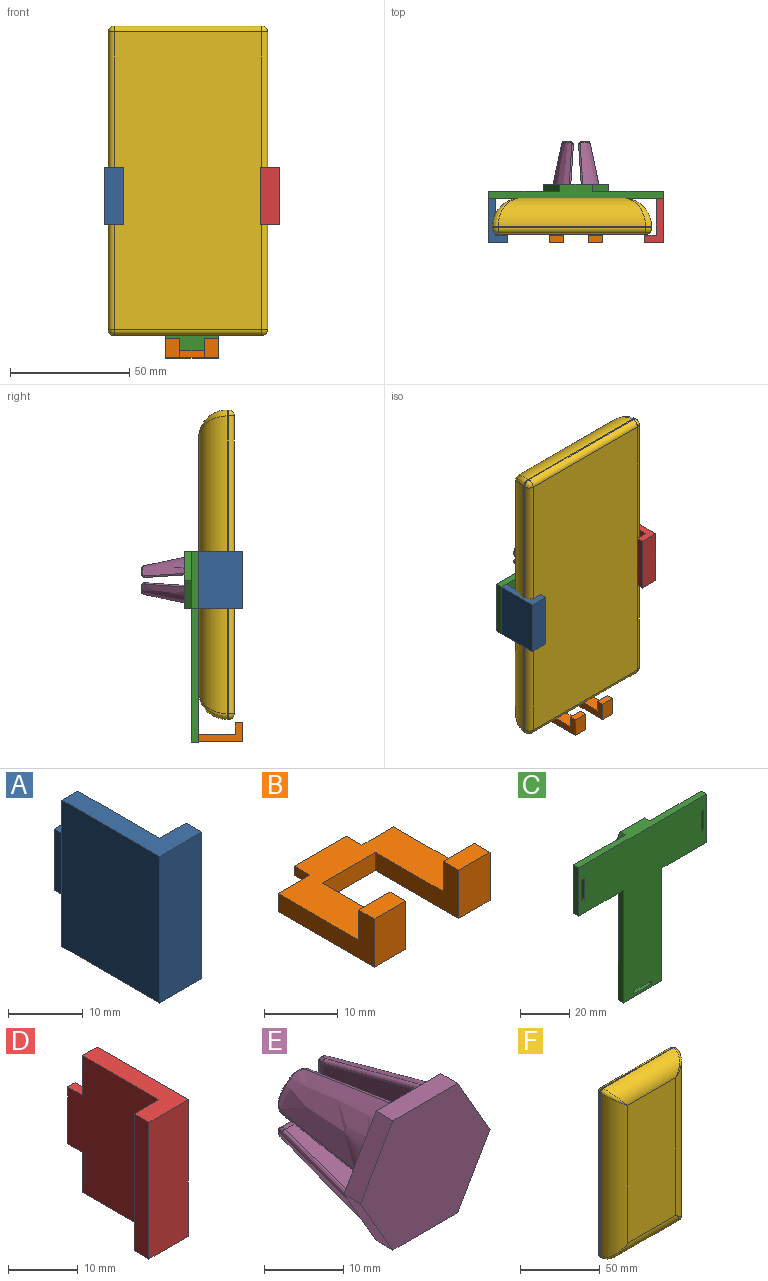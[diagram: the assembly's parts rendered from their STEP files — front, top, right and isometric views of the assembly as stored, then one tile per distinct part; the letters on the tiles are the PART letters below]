
ASSEMBLY  parts=6 mates=5
PART A: 12 faces, bbox 8x21.5x24 mm
  f0: plane 18.5x8mm, normal (0,0,-1), area 70.5mm2, adj f1,f4,f5,f6,f7,f11
  f1: plane 24x18.5mm, normal (1,0,0), area 402mm2, adj f0,f2,f3,f7,f8,f10,f11
  f2: plane 18.5x8mm, normal (0,0,1), area 70.5mm2, adj f1,f4,f5,f6,f7,f11
  f3: plane 10x1.5mm, normal (0,1,0), area 15mm2, adj f1,f8,f9,f10
  f4: plane 24x18.5mm, normal (-1,0,0), area 444mm2, adj f0,f2,f6,f11
  f5: plane 24x3mm, normal (1,0,0), area 72mm2, adj f0,f2,f6,f7
  f6: plane 24x8mm, normal (0,-1,0), area 192mm2, adj f0,f2,f4,f5
  f7: plane 24x5mm, normal (0,1,0), area 120mm2, adj f0,f1,f2,f5
  f8: plane 3x1.5mm, normal (0,0,1), area 4.5mm2, adj f1,f3,f9,f11
  f9: plane 10x3mm, normal (-1,0,0), area 30mm2, adj f3,f8,f10,f11
  f10: plane 3x1.5mm, normal (0,0,-1), area 4.5mm2, adj f1,f3,f9,f11
  f11: plane 24x3mm, normal (0,1,0), area 57mm2, adj f0,f1,f2,f4,f8,f9,f10
PART B: 18 faces, bbox 22.2x21.5x8 mm
  f0: plane 10x1.5mm, normal (0,1,0), area 15mm2, adj f1,f2,f3,f4
  f1: plane 22.2x18.5mm, normal (0,0,1), area 241.5mm2, adj f0,f3,f4,f5,f6,f7,f9,f12
  f2: plane 10x3mm, normal (0,0,-1), area 30mm2, adj f0,f3,f4,f5
  f3: plane 3x1.5mm, normal (-1,0,0), area 4.5mm2, adj f0,f1,f2,f5
  f4: plane 3x1.5mm, normal (1,0,0), area 4.5mm2, adj f0,f1,f2,f5
  f5: plane 22.2x3mm, normal (0,1,0), area 51.6mm2, adj f1,f2,f3,f4,f7,f8,f16
  f6: plane 16x8mm, normal (1,0,0), area 63mm2, adj f1,f8,f9,f10,f11,f17
  f7: plane 18.5x8mm, normal (-1,0,0), area 70.5mm2, adj f1,f5,f8,f9,f10,f11
  f8: plane 22.2x18.5mm, normal (0,0,-1), area 247.5mm2, adj f5,f6,f7,f11,f12,f15,f16,f17
  f9: plane 6x5mm, normal (0,1,0), area 30mm2, adj f1,f6,f7,f10
  f10: plane 6x3mm, normal (0,0,1), area 18mm2, adj f6,f7,f9,f11
  f11: plane 8x6mm, normal (0,-1,0), area 48mm2, adj f6,f7,f8,f10
  f12: plane 16x8mm, normal (-1,0,0), area 63mm2, adj f1,f8,f13,f14,f15,f17
  f13: plane 6x5mm, normal (0,1,0), area 30mm2, adj f1,f12,f14,f16
  f14: plane 6x3mm, normal (0,0,1), area 18mm2, adj f12,f13,f15,f16
  f15: plane 8x6mm, normal (0,-1,0), area 48mm2, adj f8,f12,f14,f16
  f16: plane 18.5x8mm, normal (1,0,0), area 70.5mm2, adj f1,f5,f8,f13,f14,f15
  f17: plane 10.2x3mm, normal (0,-1,0), area 30.6mm2, adj f1,f6,f8,f12
PART C: 35 faces, bbox 73.5x6x80 mm
  f0: plane 56x3mm, normal (-1,0,0), area 168mm2, adj f2,f3,f4,f5
  f1: plane 56x3mm, normal (1,0,0), area 168mm2, adj f2,f3,f4,f9
  f2: plane 22.2x3mm, normal (0,0,-1), area 66.6mm2, adj f0,f1,f3,f4
  f3: plane 80x73.5mm, normal (0,1,0), area 2459.9mm2, adj f0,f1,f2,f5,f6,f7,f8,f9
  f4: plane 80x73.5mm, normal (0,-1,0), area 2958.7mm2, adj f0,f1,f2,f5,f6,f7,f8,f9
  f5: plane 25.65x3mm, normal (0,0,-1), area 76.9mm2, adj f0,f3,f4,f8
  f6: plane 24x3mm, normal (1,0,0), area 72mm2, adj f3,f4,f7,f9
  f7: plane 73.5x6mm, normal (0,0,1), area 262.1mm2, adj f3,f4,f6,f8,f16,f17,f21
  f8: plane 24x3mm, normal (-1,0,0), area 72mm2, adj f3,f4,f5,f7
  f9: plane 25.65x3mm, normal (0,0,-1), area 76.9mm2, adj f1,f3,f4,f6
  f10: plane 10.1x5.83mm, normal (0.87,0,-0.5), area 35mm2, adj f11,f20,f21,f22
  f11: plane 10.1x5.83mm, normal (0.87,0,0.5), area 35mm2, adj f10,f12,f21,f22
  f12: plane 11.66x3mm, normal (0,0,1), area 35mm2, adj f11,f13,f21,f22
  f13: plane 10.1x5.83mm, normal (-0.87,0,0.5), area 35mm2, adj f12,f14,f21,f22
  f14: plane 10.1x5.83mm, normal (-0.87,0,-0.5), area 35mm2, adj f13,f20,f21,f22
  f15: plane 12x6.93mm, normal (-0.87,0,-0.5), area 41.6mm2, adj f3,f16,f19,f21
  f16: plane 12x6.93mm, normal (-0.87,0,0.5), area 41.6mm2, adj f3,f7,f15,f21
  f17: plane 12x6.93mm, normal (0.87,0,0.5), area 41.6mm2, adj f3,f7,f18,f21
  f18: plane 12x6.93mm, normal (0.87,0,-0.5), area 41.6mm2, adj f3,f17,f19,f21
  f19: plane 13.86x3mm, normal (0,0,-1), area 41.6mm2, adj f3,f15,f18,f21
  f20: plane 11.66x3mm, normal (0,0,-1), area 35mm2, adj f10,f14,f21,f22
  f21: plane 27.71x24mm, normal (0,1,0), area 145.5mm2, adj f7,f10,f11,f12,f13,f14,f15,f16
  f22: plane 23.33x20.2mm, normal (0,1,0), area 353.4mm2, adj f10,f11,f12,f13,f14,f20
  f23: plane 10.1x3mm, normal (1,0,0), area 30.3mm2, adj f3,f4,f24,f25
  f24: plane 3x1.6mm, normal (0,0,-1), area 4.8mm2, adj f3,f4,f23,f26
  f25: plane 3x1.6mm, normal (0,0,1), area 4.8mm2, adj f3,f4,f23,f26
  f26: plane 10.1x3mm, normal (-1,0,0), area 30.3mm2, adj f3,f4,f24,f25
  f27: plane 10.1x3mm, normal (0,0,1), area 30.3mm2, adj f3,f4,f28,f29
  f28: plane 3x1.6mm, normal (1,0,0), area 4.8mm2, adj f3,f4,f27,f30
  f29: plane 3x1.6mm, normal (-1,0,0), area 4.8mm2, adj f3,f4,f27,f30
  f30: plane 10.1x3mm, normal (0,0,-1), area 30.3mm2, adj f3,f4,f28,f29
  f31: plane 10.1x3mm, normal (1,0,0), area 30.3mm2, adj f3,f4,f32,f33
  f32: plane 3x1.6mm, normal (0,0,-1), area 4.8mm2, adj f3,f4,f31,f34
  f33: plane 3x1.6mm, normal (0,0,1), area 4.8mm2, adj f3,f4,f31,f34
  f34: plane 10.1x3mm, normal (-1,0,0), area 30.3mm2, adj f3,f4,f32,f33
PART D: 12 faces, bbox 8x21.5x24 mm
  f0: plane 18.5x8mm, normal (0,0,-1), area 70.5mm2, adj f1,f3,f5,f6,f7,f11
  f1: plane 24x18.5mm, normal (1,0,0), area 444mm2, adj f0,f4,f6,f11
  f2: plane 10x1.5mm, normal (0,1,0), area 15mm2, adj f3,f8,f9,f10
  f3: plane 24x18.5mm, normal (-1,0,0), area 402mm2, adj f0,f2,f4,f7,f8,f10,f11
  f4: plane 18.5x8mm, normal (0,0,1), area 70.5mm2, adj f1,f3,f5,f6,f7,f11
  f5: plane 24x3mm, normal (-1,0,0), area 72mm2, adj f0,f4,f6,f7
  f6: plane 24x8mm, normal (0,-1,0), area 192mm2, adj f0,f1,f4,f5
  f7: plane 24x5mm, normal (0,1,0), area 120mm2, adj f0,f3,f4,f5
  f8: plane 3x1.5mm, normal (0,0,-1), area 4.5mm2, adj f2,f3,f9,f11
  f9: plane 10x3mm, normal (1,0,0), area 30mm2, adj f2,f8,f10,f11
  f10: plane 3x1.5mm, normal (0,0,1), area 4.5mm2, adj f2,f3,f9,f11
  f11: plane 24x3mm, normal (0,1,0), area 57mm2, adj f0,f1,f3,f4,f8,f9,f10
PART E: 60 faces, bbox 23.2x23.4x20.6 mm
  f0: bspline ~17.61x8.12mm, area 143.4mm2, adj f4,f18,f19,f20,f48,f52
  f1: bspline ~17.61x8.12mm, area 143.4mm2, adj f4,f22,f23,f24,f43,f47
  f2: bspline ~17.61x8.12mm, area 143.4mm2, adj f4,f26,f27,f28,f38,f42
  f3: bspline ~17.61x8.12mm, area 143.4mm2, adj f4,f30,f31,f32,f33,f37
  f4: plane 23.15x20.06mm, normal (0,1,0), area 188.5mm2, adj f0,f1,f2,f3,f6,f7,f9,f10
  f5: plane 2.36x2.36mm, normal (0,1,0), area 3.3mm2, adj f31,f34,f36
  f6: plane 16.4x7.48mm, normal (-1,-0.07,0), area 85.4mm2, adj f4,f29,f32,f34
  f7: plane 16.4x7.48mm, normal (0,-0.07,-1), area 85.4mm2, adj f4,f29,f30,f36
  f8: plane 2.36x2.36mm, normal (0,1,0), area 3.3mm2, adj f27,f39,f41
  f9: plane 16.4x7.48mm, normal (1,-0.07,0), area 85.4mm2, adj f4,f25,f28,f39
  f10: plane 16.4x7.48mm, normal (0,-0.07,-1), area 85.4mm2, adj f4,f25,f26,f41
  f11: plane 2.36x2.36mm, normal (0,1,0), area 3.3mm2, adj f23,f44,f46
  f12: plane 16.4x7.48mm, normal (-1,-0.07,0), area 85.4mm2, adj f4,f21,f24,f44
  f13: plane 16.4x7.48mm, normal (0,-0.07,1), area 85.4mm2, adj f4,f21,f22,f46
  f14: plane 2.36x2.36mm, normal (0,1,0), area 3.3mm2, adj f19,f49,f51
  f15: plane 16.4x7.48mm, normal (0,-0.07,1), area 85.4mm2, adj f4,f17,f20,f49
  f16: plane 16.4x7.48mm, normal (1,-0.07,0), area 85.4mm2, adj f4,f17,f18,f51
  f17: cylinder r=0.5mm len=16.41mm, axis (-0.07,-1,-0.07), area 12.9mm2, adj f4,f15,f16,f50
  f18: bspline ~22.72x5.45mm, area 15.7mm2, adj f0,f4,f16,f52
  f19: bspline ~3.89x3.54mm, area 2.4mm2, adj f0,f14,f48,f52
  f20: bspline ~22.72x5.45mm, area 15.7mm2, adj f0,f4,f15,f48
  f21: cylinder r=0.5mm len=16.41mm, axis (0.07,-1,-0.07), area 12.9mm2, adj f4,f12,f13,f45
  f22: bspline ~22.72x5.45mm, area 15.7mm2, adj f1,f4,f13,f47
  f23: bspline ~3.89x3.54mm, area 2.4mm2, adj f1,f11,f43,f47
  f24: bspline ~22.72x5.45mm, area 15.7mm2, adj f1,f4,f12,f43
  f25: cylinder r=0.5mm len=16.41mm, axis (-0.07,-1,0.07), area 12.9mm2, adj f4,f9,f10,f40
  f26: bspline ~22.72x5.45mm, area 15.7mm2, adj f2,f4,f10,f42
  f27: bspline ~3.89x3.54mm, area 2.4mm2, adj f2,f8,f38,f42
  f28: bspline ~22.72x5.45mm, area 15.7mm2, adj f2,f4,f9,f38
  f29: cylinder r=0.5mm len=16.41mm, axis (-0.07,1,-0.07), area 12.9mm2, adj f4,f6,f7,f35
  f30: bspline ~20.18x4.91mm, area 15.7mm2, adj f3,f4,f7,f37
  f31: bspline ~3.62x3.43mm, area 2.4mm2, adj f3,f5,f33,f37
  f32: bspline ~20.18x4.91mm, area 15.7mm2, adj f3,f4,f6,f33
  f33: bspline ~2.03x1.75mm, area 1.9mm2, adj f3,f31,f32,f34
  f34: cylinder r=1.5mm len=4mm, axis (0,0,-1), area 7.8mm2, adj f5,f6,f33,f35
  f35: bspline ~1.76x1.5mm, area 0.9mm2, adj f29,f34,f36
  f36: cylinder r=1.5mm len=4mm, axis (-1,0,0), area 7.8mm2, adj f5,f7,f35,f37
  f37: bspline ~1.99x1.93mm, area 1.9mm2, adj f3,f30,f31,f36
  f38: bspline ~1.99x1.93mm, area 1.9mm2, adj f2,f27,f28,f39
  f39: cylinder r=1.5mm len=4mm, axis (0,0,-1), area 7.8mm2, adj f8,f9,f38,f40
  f40: bspline ~1.76x1.5mm, area 0.9mm2, adj f25,f39,f41
  f41: cylinder r=1.5mm len=4mm, axis (1,0,0), area 7.8mm2, adj f8,f10,f40,f42
  f42: bspline ~2.03x1.75mm, area 1.9mm2, adj f2,f26,f27,f41
  f43: bspline ~1.99x1.93mm, area 1.9mm2, adj f1,f23,f24,f44
  f44: cylinder r=1.5mm len=4mm, axis (0,0,1), area 7.8mm2, adj f11,f12,f43,f45
  f45: bspline ~1.76x1.5mm, area 0.9mm2, adj f21,f44,f46
  f46: cylinder r=1.5mm len=4mm, axis (-1,0,0), area 7.8mm2, adj f11,f13,f45,f47
  f47: bspline ~2.03x1.75mm, area 1.9mm2, adj f1,f22,f23,f46
  f48: bspline ~1.99x1.93mm, area 1.9mm2, adj f0,f19,f20,f49
  f49: cylinder r=1.5mm len=4mm, axis (1,0,0), area 7.8mm2, adj f14,f15,f48,f50
  f50: bspline ~1.76x1.5mm, area 0.9mm2, adj f17,f49,f51
  f51: cylinder r=1.5mm len=4mm, axis (0,0,1), area 7.8mm2, adj f14,f16,f50,f52
  f52: bspline ~2.03x1.75mm, area 1.9mm2, adj f0,f18,f19,f51
  f53: plane 11.55x3mm, normal (0,0,1), area 34.6mm2, adj f4,f54,f58,f59
  f54: plane 10x5.77mm, normal (0.87,0,0.5), area 34.6mm2, adj f4,f53,f55,f59
  f55: plane 10x5.77mm, normal (0.87,0,-0.5), area 34.6mm2, adj f4,f54,f56,f59
  f56: plane 11.55x3mm, normal (0,0,-1), area 34.6mm2, adj f4,f55,f57,f59
  f57: plane 10x5.77mm, normal (-0.87,0,-0.5), area 34.6mm2, adj f4,f56,f58,f59
  f58: plane 10x5.77mm, normal (-0.87,0,0.5), area 34.6mm2, adj f4,f53,f57,f59
  f59: plane 23.09x20mm, normal (0,-1,0), area 346.4mm2, adj f53,f54,f55,f56,f57,f58
PART F: 26 faces, bbox 67x15x130 mm
  f0: plane 62x0.5mm, normal (0,0,1), area 31mm2, adj f6,f9,f11,f20
  f1: plane 125x0.5mm, normal (-1,0,0), area 62.5mm2, adj f6,f7,f12,f19
  f2: plane 62x0.5mm, normal (0,0,-1), area 31mm2, adj f7,f8,f16,f23
  f3: plane 125x0.5mm, normal (1,0,0), area 62.5mm2, adj f8,f9,f15,f24
  f4: plane 106x43mm, normal (0,-1,0), area 4558mm2, adj f19,f20,f23,f24
  f5: plane 125x62mm, normal (0,1,0), area 7750mm2, adj f11,f12,f15,f16
  f6: cylinder r=2.5mm len=2.5mm, axis (0,-1,0), area 2mm2, adj f0,f1,f10,f18
  f7: cylinder r=2.5mm len=2.5mm, axis (0,1,0), area 2mm2, adj f1,f2,f14,f21
  f8: cylinder r=2.5mm len=2.5mm, axis (0,-1,0), area 2mm2, adj f2,f3,f17,f25
  f9: cylinder r=2.5mm len=2.5mm, axis (0,1,0), area 2mm2, adj f0,f3,f13,f22
  f10: sphere r=2.5mm, area 9.8mm2, adj f6,f11,f12
  f11: cylinder r=2.5mm len=62mm, axis (-1,0,0), area 243.5mm2, adj f0,f5,f10,f13
  f12: cylinder r=2.5mm len=125mm, axis (0,0,-1), area 490.9mm2, adj f1,f5,f10,f14
  f13: sphere r=2.5mm, area 9.8mm2, adj f9,f11,f15
  f14: sphere r=2.5mm, area 9.8mm2, adj f7,f12,f16
  f15: cylinder r=2.5mm len=125mm, axis (0,0,1), area 490.9mm2, adj f3,f5,f13,f17
  f16: cylinder r=2.5mm len=62mm, axis (1,0,0), area 243.5mm2, adj f2,f5,f14,f17
  f17: sphere r=2.5mm, area 9.8mm2, adj f8,f15,f16
  f18: bspline ~13.88x12mm, area 50.9mm2, adj f6,f19,f20
  f19: cylinder r=12mm len=125mm, axis (0,0,1), area 2226.1mm2, adj f1,f4,f18,f21
  f20: cylinder r=12mm len=62mm, axis (1,0,0), area 1038.5mm2, adj f0,f4,f18,f22
  f21: bspline ~13.88x12mm, area 50.9mm2, adj f7,f19,f23
  f22: bspline ~13.88x12mm, area 50.9mm2, adj f9,f20,f24
  f23: cylinder r=12mm len=62mm, axis (-1,0,0), area 1038.5mm2, adj f2,f4,f21,f25
  f24: cylinder r=12mm len=125mm, axis (0,0,-1), area 2226.1mm2, adj f3,f4,f22,f25
  f25: bspline ~13.88x12mm, area 50.9mm2, adj f8,f23,f24
PLACE A t=(-81.2,-40.39,27.55)mm
PLACE B t=(-94.2,-40.39,40.65)mm
PLACE C t=(-94.2,-40.39,27.55)mm
PLACE D t=(-107.2,-40.39,27.55)mm
PLACE E t=(-94.2,-57.39,27.55)mm
PLACE F rot(axis=(1,0,0),180deg) t=(-232.27,-75.39,-8.84)mm
MATE fastened B.f0 <-> C.f3  axis (0,1,0) through (-94.2,-57.39,-37.35)mm
MATE fastened E.f59 <-> C.f22  axis (0,-1,0) through (-94.2,-57.39,27.55)mm
MATE planar C.f4 <-> F.f4  axis (0,-1,0) through (-94.2,-60.39,11.11)mm
MATE fastened D.f2 <-> C.f3  axis (0,1,0) through (-58.95,-57.39,27.55)mm
MATE fastened A.f3 <-> C.f3  axis (0,1,0) through (-129.45,-57.39,27.55)mm
